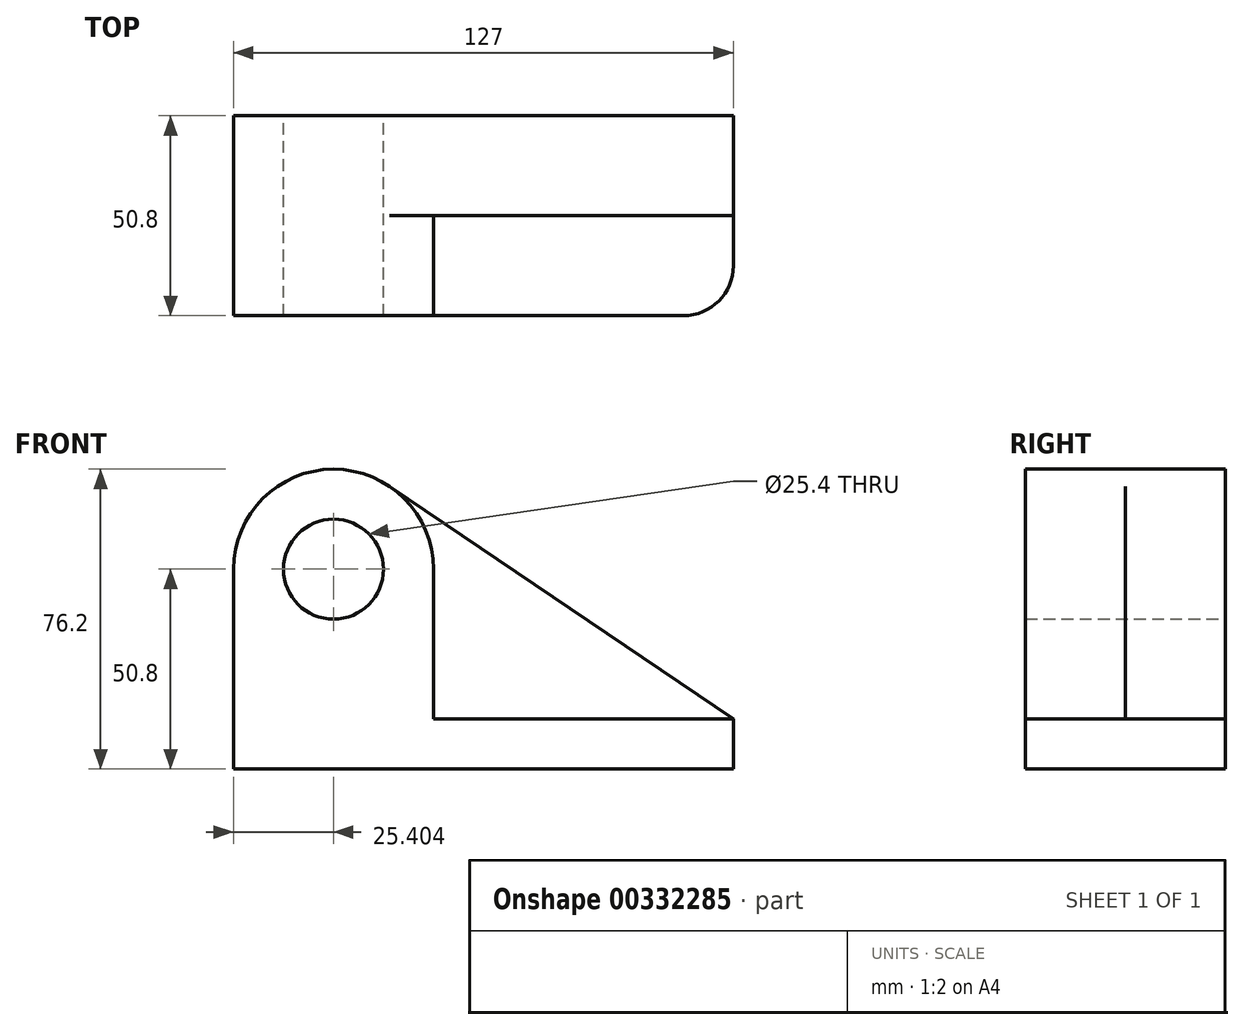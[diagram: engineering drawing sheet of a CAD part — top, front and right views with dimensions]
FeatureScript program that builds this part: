
annotation { "Feature Type Name" : "Feature", "Feature Type Description" : "" }
export const myFeature = defineFeature(function(context is Context, id is Id, definition is map)
    precondition{}
    {
        {
            var Q0;
            Q0=qCreatedBy(makeId("Front.planeOp"),FACE);
            var sketch = newSketch(context, id + "F0", { "sketchPlane" : qUnion([Q0])});
            skCircle(sketch, "E0", {"center": v(-38.37, 50.8) * mm, "radius": 12.7 * mm});
            skArc(sketch, "E1", {"start": v(-24.13, 71.83) * mm, "mid": v(-50.27, 73.24) * mm, "end": v(-63.77, 50.8) * mm});
            skLineSegment(sketch, "E2", {"start": v(-63.77, 50.8) * mm, "end": v(-63.77, 0) * mm});
            skLineSegment(sketch, "E3", {"start": v(-63.77, 0) * mm, "end": v(63.23, 0) * mm});
            skLineSegment(sketch, "E4", {"start": v(63.23, 0) * mm, "end": v(63.23, 12.7) * mm});
            skLineSegment(sketch, "E5", {"start": v(63.23, 12.7) * mm, "end": v(-24.13, 71.83) * mm});
            skSolve(sketch);
        }
        {
            var Q0;
            Q0=makeQuery(id+"F0.imprint","IMPRINT",FACE,{"disambiguationData":[TD([[makeQuery(id+"F0.imprint","IMPRINT",EDGE,{"derivedFrom":sQuery(id+"F0.wireOp",EDGE,"E0")}),-1.0]])]});
            extrude(context, id + "F1", {"entities" : qUnion([Q0]), "depth" : 25.4 * mm});
        }
        {
            var Q0;
            Q0=makeQuery(id+"F1.opExtrude","CAP_FACE",FACE,{"disambiguationData":[OSD([sQuery(id+"F0.wireOp",EDGE,"E0"),sQuery(id+"F0.wireOp",EDGE,"E1"),sQuery(id+"F0.wireOp",EDGE,"E2"),sQuery(id+"F0.wireOp",EDGE,"E3"),sQuery(id+"F0.wireOp",EDGE,"E4"),sQuery(id+"F0.wireOp",EDGE,"E5")])],"isStart":false});
            var sketch = newSketch(context, id + "F2", { "sketchPlane" : qUnion([Q0])});
            skCircle(sketch, "E6", {"center": v(-38.37, 50.8) * mm, "radius": 12.7 * mm});
            skArc(sketch, "E7", {"start": v(-12.97, 50.8) * mm, "mid": v(-38.37, 76.2) * mm, "end": v(-63.77, 50.8) * mm});
            skLineSegment(sketch, "E8.left", {"start": v(63.23, 12.7) * mm, "end": v(63.23, 0) * mm});
            skLineSegment(sketch, "E8.right", {"start": v(-63.77, 12.7) * mm, "end": v(-63.77, 0) * mm});
            skLineSegment(sketch, "E9.bottom", {"start": v(63.23, 12.7) * mm, "end": v(-12.97, 12.7) * mm});
            skLineSegment(sketch, "E9.top", {"start": v(63.23, 0) * mm, "end": v(-63.77, 0) * mm});
            skLineSegment(sketch, "E10", {"start": v(-63.77, 50.8) * mm, "end": v(-63.77, 12.7) * mm});
            skLineSegment(sketch, "E11", {"start": v(-12.97, 50.8) * mm, "end": v(-12.97, 12.7) * mm});
            skSolve(sketch);
        }
        {
            var Q0;
            Q0=makeQuery(id+"F2.imprint","IMPRINT",FACE,{"disambiguationData":[TD([[makeQuery(id+"F2.imprint","IMPRINT",EDGE,{"derivedFrom":sQuery(id+"F2.wireOp",EDGE,"E6")}),-1.0]])]});
            extrude(context, id + "F3", {"entities" : qUnion([Q0]), "operationType" : NewBodyOperationType.ADD, "depth" : 25.4 * mm});
        }
        {
            var Q0;
            Q0=makeQuery(id+"F3.opExtrude","CAP_EDGE",EDGE,{"disambiguationData":[OSD([sQuery(id+"F2.wireOp",EDGE,"E8.left")])],"isStart":false});
            fillet(context, id + "F4", {"entities" : qUnion([Q0]), "radius" : 12.7 * mm, "tangentPropagation" : true, "allowEdgeOverflow" : false});
        }
    });
